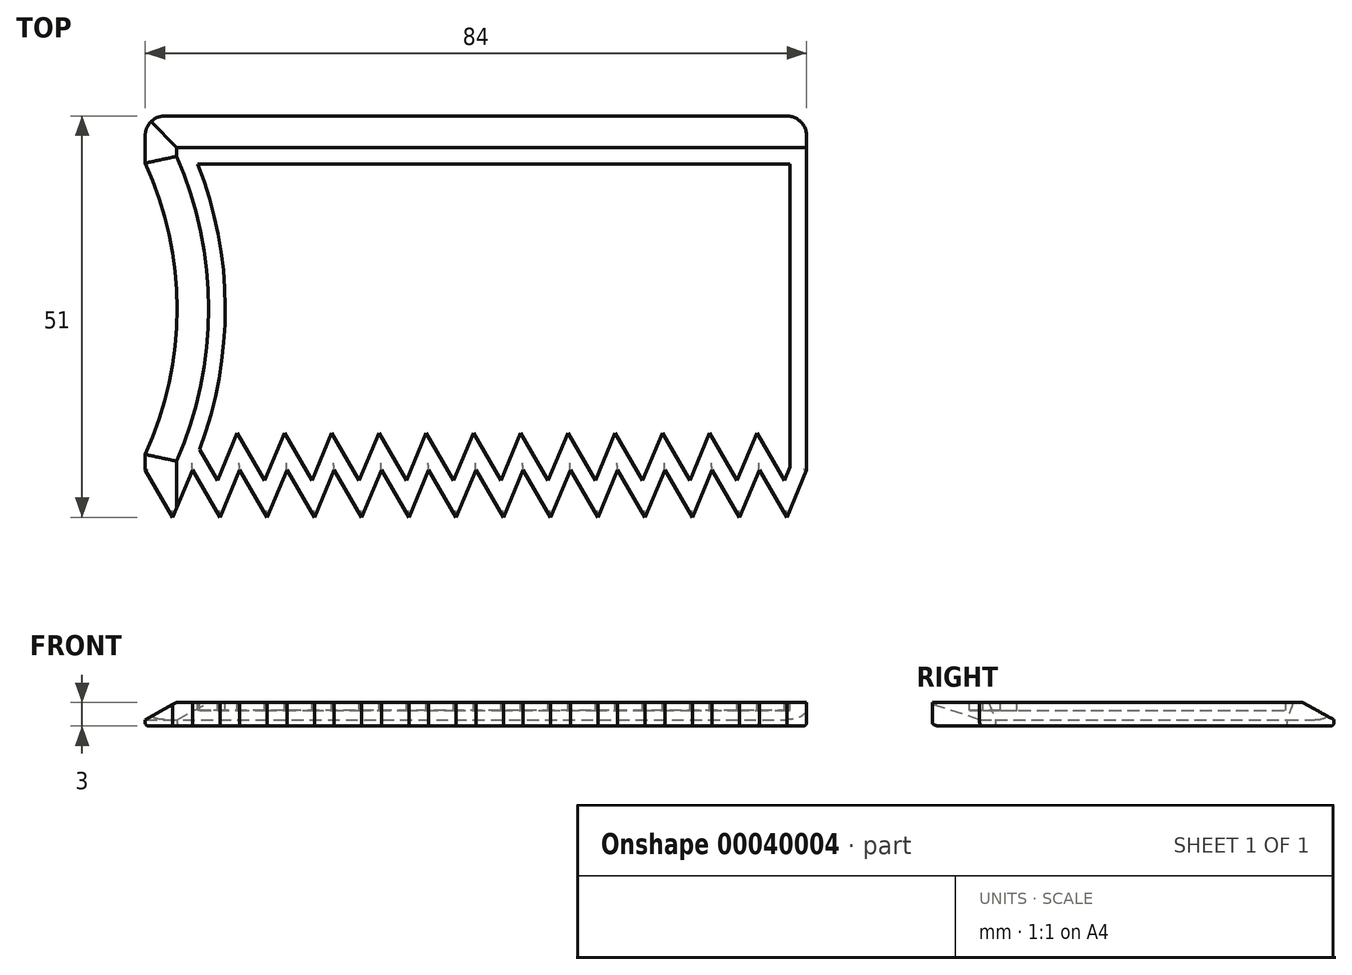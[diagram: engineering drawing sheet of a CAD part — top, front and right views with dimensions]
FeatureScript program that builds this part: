
annotation { "Feature Type Name" : "Feature", "Feature Type Description" : "" }
export const myFeature = defineFeature(function(context is Context, id is Id, definition is map)
    precondition{}
    {
        {
            var Q0;
            Q0=qCreatedBy(makeId("Top.planeOp"),FACE);
            var sketch = newSketch(context, id + "F0", { "sketchPlane" : qUnion([Q0])});
            skLineSegment(sketch, "E0.bottom", {"start": v(84, 51) * mm, "end": v(0, 51) * mm});
            skLineSegment(sketch, "E0.top", {"start": v(81.5, 0) * mm, "end": v(3.5, 0) * mm, "construction": true});
            skLineSegment(sketch, "E0.left", {"start": v(84, 51) * mm, "end": v(84, 6) * mm});
            skLineSegment(sketch, "E0.right", {"start": v(0, 51) * mm, "end": v(0, 6) * mm, "construction": true});
            skLineSegment(sketch, "E1", {"start": v(84, 6) * mm, "end": v(0, 6) * mm, "construction": true});
            skLineSegment(sketch, "E2", {"start": v(84, 6) * mm, "end": v(81.5, 0) * mm});
            skLineSegment(sketch, "E3", {"start": v(81.5, 0) * mm, "end": v(78, 6) * mm});
            skLineSegment(sketch, "E4.1.0.0", {"start": v(78, 6) * mm, "end": v(75.5, 0) * mm});
            skLineSegment(sketch, "E4.1.0.1", {"start": v(75.5, 0) * mm, "end": v(72, 6) * mm});
            skLineSegment(sketch, "E4.2.0.0", {"start": v(72, 6) * mm, "end": v(69.5, 0) * mm});
            skLineSegment(sketch, "E4.2.0.1", {"start": v(69.5, 0) * mm, "end": v(66, 6) * mm});
            skLineSegment(sketch, "E4.3.0.0", {"start": v(66, 6) * mm, "end": v(63.5, 0) * mm});
            skLineSegment(sketch, "E4.3.0.1", {"start": v(63.5, 0) * mm, "end": v(60, 6) * mm});
            skLineSegment(sketch, "E4.4.0.0", {"start": v(60, 6) * mm, "end": v(57.5, 0) * mm});
            skLineSegment(sketch, "E4.4.0.1", {"start": v(57.5, 0) * mm, "end": v(54, 6) * mm});
            skLineSegment(sketch, "E4.5.0.0", {"start": v(54, 6) * mm, "end": v(51.5, 0) * mm});
            skLineSegment(sketch, "E4.5.0.1", {"start": v(51.5, 0) * mm, "end": v(48, 6) * mm});
            skLineSegment(sketch, "E4.6.0.0", {"start": v(48, 6) * mm, "end": v(45.5, 0) * mm});
            skLineSegment(sketch, "E4.6.0.1", {"start": v(45.5, 0) * mm, "end": v(42, 6) * mm});
            skLineSegment(sketch, "E4.7.0.0", {"start": v(42, 6) * mm, "end": v(39.5, 0) * mm});
            skLineSegment(sketch, "E4.7.0.1", {"start": v(39.5, 0) * mm, "end": v(36, 6) * mm});
            skLineSegment(sketch, "E4.8.0.0", {"start": v(36, 6) * mm, "end": v(33.5, 0) * mm});
            skLineSegment(sketch, "E4.8.0.1", {"start": v(33.5, 0) * mm, "end": v(30, 6) * mm});
            skLineSegment(sketch, "E4.9.0.0", {"start": v(30, 6) * mm, "end": v(27.5, 0) * mm});
            skLineSegment(sketch, "E4.9.0.1", {"start": v(27.5, 0) * mm, "end": v(24, 6) * mm});
            skLineSegment(sketch, "E4.10.0.0", {"start": v(24, 6) * mm, "end": v(21.5, 0) * mm});
            skLineSegment(sketch, "E4.10.0.1", {"start": v(21.5, 0) * mm, "end": v(18, 6) * mm});
            skLineSegment(sketch, "E4.11.0.0", {"start": v(18, 6) * mm, "end": v(15.5, 0) * mm});
            skLineSegment(sketch, "E4.11.0.1", {"start": v(15.5, 0) * mm, "end": v(12, 6) * mm});
            skLineSegment(sketch, "E4.12.0.0", {"start": v(12, 6) * mm, "end": v(9.5, 0) * mm});
            skLineSegment(sketch, "E4.12.0.1", {"start": v(9.5, 0) * mm, "end": v(6, 6) * mm});
            skLineSegment(sketch, "E4.13.0.0", {"start": v(6, 6) * mm, "end": v(3.5, 0) * mm});
            skLineSegment(sketch, "E4.13.0.1", {"start": v(3.5, 0) * mm, "end": v(0, 6) * mm});
            skLineSegment(sketch, "E4.direction1", {"start": v(84, 6) * mm, "end": v(78, 6) * mm, "construction": true});
            skLineSegment(sketch, "E5", {"start": v(0, 6) * mm, "end": v(0, 8) * mm});
            skArc(sketch, "E6", {"start": v(0, 8) * mm, "mid": v(4.07, 26.5) * mm, "end": v(0, 45) * mm});
            skLineSegment(sketch, "E7", {"start": v(0, 45) * mm, "end": v(0, 51) * mm});
            skLineSegment(sketch, "E8", {"start": v(0, 6) * mm, "end": v(0, 0) * mm, "construction": true});
            skSolve(sketch);
        }
        {
            var Q0;
            Q0=qSketchRegion(id+"F0",true);
            extrude(context, id + "F1", {"entities" : qUnion([Q0]), "depth" : 3 * mm});
        }
        {
            var Q0;
            Q0=makeQuery(id+"F1.opExtrude","CAP_EDGE",EDGE,{"disambiguationData":[OSD([sQuery(id+"F0.wireOp",EDGE,"E5")])],"isStart":false});
            var Q1;
            Q1=makeQuery(id+"F1.opExtrude","CAP_EDGE",EDGE,{"disambiguationData":[OSD([sQuery(id+"F0.wireOp",EDGE,"E6")])],"isStart":false});
            var Q2;
            Q2=makeQuery(id+"F1.opExtrude","CAP_EDGE",EDGE,{"disambiguationData":[OSD([sQuery(id+"F0.wireOp",EDGE,"E0.bottom")])],"isStart":false});
            var Q3;
            Q3=makeQuery(id+"F1.opExtrude","CAP_EDGE",EDGE,{"disambiguationData":[OSD([sQuery(id+"F0.wireOp",EDGE,"E7")])],"isStart":false});
            chamfer(context, id + "F2", {"entities" : qUnion([Q0, Q1, Q2, Q3]), "chamferType" : ChamferType.TWO_OFFSETS, "width1" : 2.2 * mm, "oppositeDirection" : false, "width2" : 4 * mm, "tangentPropagation" : true});
        }
        {
            var Q0;
            Q0=makeQuery(id+"F1.opExtrude","SWEPT_EDGE",EDGE,{"disambiguationData":[OSD([sQuery(id+"F0.wireOp",EDGE,"E0.bottom"),sQuery(id+"F0.wireOp",EDGE,"E7")])]});
            var Q1;
            Q1=makeQuery(id+"F1.opExtrude","SWEPT_EDGE",EDGE,{"disambiguationData":[OSD([sQuery(id+"F0.wireOp",EDGE,"E0.bottom"),sQuery(id+"F0.wireOp",EDGE,"E0.left")])]});
            fillet(context, id + "F3", {"entities" : qUnion([Q0, Q1]), "radius" : 2.5 * mm, "tangentPropagation" : true, "allowEdgeOverflow" : false});
        }
        {
            var Q0;
            Q0=makeQuery(id+"F1.opExtrude","CAP_FACE",FACE,{"disambiguationData":[OSD([sQuery(id+"F0.wireOp",EDGE,"E0.bottom"),sQuery(id+"F0.wireOp",EDGE,"E0.left"),sQuery(id+"F0.wireOp",EDGE,"E2"),sQuery(id+"F0.wireOp",EDGE,"E3"),sQuery(id+"F0.wireOp",EDGE,"E4.1.0.0"),sQuery(id+"F0.wireOp",EDGE,"E4.1.0.1"),sQuery(id+"F0.wireOp",EDGE,"E4.2.0.0"),sQuery(id+"F0.wireOp",EDGE,"E4.2.0.1"),sQuery(id+"F0.wireOp",EDGE,"E4.3.0.0"),sQuery(id+"F0.wireOp",EDGE,"E4.3.0.1"),sQuery(id+"F0.wireOp",EDGE,"E4.4.0.0"),sQuery(id+"F0.wireOp",EDGE,"E4.4.0.1"),sQuery(id+"F0.wireOp",EDGE,"E4.5.0.0"),sQuery(id+"F0.wireOp",EDGE,"E4.5.0.1"),sQuery(id+"F0.wireOp",EDGE,"E4.6.0.0"),sQuery(id+"F0.wireOp",EDGE,"E4.6.0.1"),sQuery(id+"F0.wireOp",EDGE,"E4.7.0.0"),sQuery(id+"F0.wireOp",EDGE,"E4.7.0.1"),sQuery(id+"F0.wireOp",EDGE,"E4.8.0.0"),sQuery(id+"F0.wireOp",EDGE,"E4.8.0.1"),sQuery(id+"F0.wireOp",EDGE,"E4.9.0.0"),sQuery(id+"F0.wireOp",EDGE,"E4.9.0.1"),sQuery(id+"F0.wireOp",EDGE,"E4.10.0.0"),sQuery(id+"F0.wireOp",EDGE,"E4.10.0.1"),sQuery(id+"F0.wireOp",EDGE,"E4.11.0.0"),sQuery(id+"F0.wireOp",EDGE,"E4.11.0.1"),sQuery(id+"F0.wireOp",EDGE,"E4.12.0.0"),sQuery(id+"F0.wireOp",EDGE,"E4.12.0.1"),sQuery(id+"F0.wireOp",EDGE,"E4.13.0.0"),sQuery(id+"F0.wireOp",EDGE,"E4.13.0.1"),sQuery(id+"F0.wireOp",EDGE,"E5"),sQuery(id+"F0.wireOp",EDGE,"E6"),sQuery(id+"F0.wireOp",EDGE,"E7")])],"isStart":false});
            var sketch = newSketch(context, id + "F4", { "sketchPlane" : qUnion([Q0])});
            skLineSegment(sketch, "E9.0", {"start": v(81.9, 6.42) * mm, "end": v(81.9, 44.9) * mm});
            skLineSegment(sketch, "E9.1", {"start": v(81.19, 4.7) * mm, "end": v(81.9, 6.42) * mm});
            skLineSegment(sketch, "E9.2", {"start": v(77.69, 10.7) * mm, "end": v(81.19, 4.7) * mm});
            skLineSegment(sketch, "E9.3", {"start": v(75.19, 4.7) * mm, "end": v(77.69, 10.7) * mm});
            skLineSegment(sketch, "E9.4", {"start": v(71.69, 10.7) * mm, "end": v(75.19, 4.7) * mm});
            skLineSegment(sketch, "E9.5", {"start": v(69.19, 4.7) * mm, "end": v(71.69, 10.7) * mm});
            skLineSegment(sketch, "E9.6", {"start": v(65.69, 10.7) * mm, "end": v(69.19, 4.7) * mm});
            skLineSegment(sketch, "E9.7", {"start": v(81.9, 44.9) * mm, "end": v(6.68, 44.9) * mm});
            skArc(sketch, "E9.8", {"start": v(6.68, 44.9) * mm, "mid": v(10.17, 26.8) * mm, "end": v(6.89, 8.65) * mm});
            skLineSegment(sketch, "E9.9", {"start": v(6.89, 8.65) * mm, "end": v(9.19, 4.7) * mm});
            skLineSegment(sketch, "E9.10", {"start": v(9.19, 4.7) * mm, "end": v(11.69, 10.7) * mm});
            skLineSegment(sketch, "E9.11", {"start": v(11.69, 10.7) * mm, "end": v(15.19, 4.7) * mm});
            skLineSegment(sketch, "E9.12", {"start": v(15.19, 4.7) * mm, "end": v(17.69, 10.7) * mm});
            skLineSegment(sketch, "E9.13", {"start": v(17.69, 10.7) * mm, "end": v(21.19, 4.7) * mm});
            skLineSegment(sketch, "E9.14", {"start": v(21.19, 4.7) * mm, "end": v(23.69, 10.7) * mm});
            skLineSegment(sketch, "E9.15", {"start": v(23.69, 10.7) * mm, "end": v(27.19, 4.7) * mm});
            skLineSegment(sketch, "E9.16", {"start": v(27.19, 4.7) * mm, "end": v(29.69, 10.7) * mm});
            skLineSegment(sketch, "E9.17", {"start": v(29.69, 10.7) * mm, "end": v(33.19, 4.7) * mm});
            skLineSegment(sketch, "E9.18", {"start": v(33.19, 4.7) * mm, "end": v(35.69, 10.7) * mm});
            skLineSegment(sketch, "E9.19", {"start": v(35.69, 10.7) * mm, "end": v(39.19, 4.7) * mm});
            skLineSegment(sketch, "E9.20", {"start": v(39.19, 4.7) * mm, "end": v(41.69, 10.7) * mm});
            skLineSegment(sketch, "E9.21", {"start": v(41.69, 10.7) * mm, "end": v(45.19, 4.7) * mm});
            skLineSegment(sketch, "E9.22", {"start": v(45.19, 4.7) * mm, "end": v(47.69, 10.7) * mm});
            skLineSegment(sketch, "E9.23", {"start": v(47.69, 10.7) * mm, "end": v(51.19, 4.7) * mm});
            skLineSegment(sketch, "E9.24", {"start": v(51.19, 4.7) * mm, "end": v(53.69, 10.7) * mm});
            skLineSegment(sketch, "E9.25", {"start": v(53.69, 10.7) * mm, "end": v(57.19, 4.7) * mm});
            skLineSegment(sketch, "E9.26", {"start": v(57.19, 4.7) * mm, "end": v(59.69, 10.7) * mm});
            skLineSegment(sketch, "E9.27", {"start": v(59.69, 10.7) * mm, "end": v(63.19, 4.7) * mm});
            skLineSegment(sketch, "E9.28", {"start": v(63.19, 4.7) * mm, "end": v(65.69, 10.7) * mm});
            skSolve(sketch);
        }
        {
            var Q0;
            Q0=makeQuery(id+"F4.imprint","IMPRINT",FACE,{"disambiguationData":[TD([[makeQuery(id+"F4.imprint","IMPRINT",EDGE,{"derivedFrom":sQuery(id+"F4.wireOp",EDGE,"E9.0")}),1.0]])]});
            extrude(context, id + "F5", {"entities" : qUnion([Q0]), "operationType" : NewBodyOperationType.REMOVE, "oppositeDirection" : true, "depth" : 1 * mm});
        }
        {
            var Q0;
            Q0=makeQuery(id+"F1.opExtrude","CAP_FACE",FACE,{"disambiguationData":[OSD([sQuery(id+"F0.wireOp",EDGE,"E0.bottom"),sQuery(id+"F0.wireOp",EDGE,"E0.left"),sQuery(id+"F0.wireOp",EDGE,"E2"),sQuery(id+"F0.wireOp",EDGE,"E3"),sQuery(id+"F0.wireOp",EDGE,"E4.1.0.0"),sQuery(id+"F0.wireOp",EDGE,"E4.1.0.1"),sQuery(id+"F0.wireOp",EDGE,"E4.2.0.0"),sQuery(id+"F0.wireOp",EDGE,"E4.2.0.1"),sQuery(id+"F0.wireOp",EDGE,"E4.3.0.0"),sQuery(id+"F0.wireOp",EDGE,"E4.3.0.1"),sQuery(id+"F0.wireOp",EDGE,"E4.4.0.0"),sQuery(id+"F0.wireOp",EDGE,"E4.4.0.1"),sQuery(id+"F0.wireOp",EDGE,"E4.5.0.0"),sQuery(id+"F0.wireOp",EDGE,"E4.5.0.1"),sQuery(id+"F0.wireOp",EDGE,"E4.6.0.0"),sQuery(id+"F0.wireOp",EDGE,"E4.6.0.1"),sQuery(id+"F0.wireOp",EDGE,"E4.7.0.0"),sQuery(id+"F0.wireOp",EDGE,"E4.7.0.1"),sQuery(id+"F0.wireOp",EDGE,"E4.8.0.0"),sQuery(id+"F0.wireOp",EDGE,"E4.8.0.1"),sQuery(id+"F0.wireOp",EDGE,"E4.9.0.0"),sQuery(id+"F0.wireOp",EDGE,"E4.9.0.1"),sQuery(id+"F0.wireOp",EDGE,"E4.10.0.0"),sQuery(id+"F0.wireOp",EDGE,"E4.10.0.1"),sQuery(id+"F0.wireOp",EDGE,"E4.11.0.0"),sQuery(id+"F0.wireOp",EDGE,"E4.11.0.1"),sQuery(id+"F0.wireOp",EDGE,"E4.12.0.0"),sQuery(id+"F0.wireOp",EDGE,"E4.12.0.1"),sQuery(id+"F0.wireOp",EDGE,"E4.13.0.0"),sQuery(id+"F0.wireOp",EDGE,"E4.13.0.1"),sQuery(id+"F0.wireOp",EDGE,"E5"),sQuery(id+"F0.wireOp",EDGE,"E6"),sQuery(id+"F0.wireOp",EDGE,"E7")])],"isStart":true});
            fillet(context, id + "F6", {"entities" : qUnion([Q0]), "radius" : .4 * mm, "tangentPropagation" : true, "allowEdgeOverflow" : false});
        }
    });
